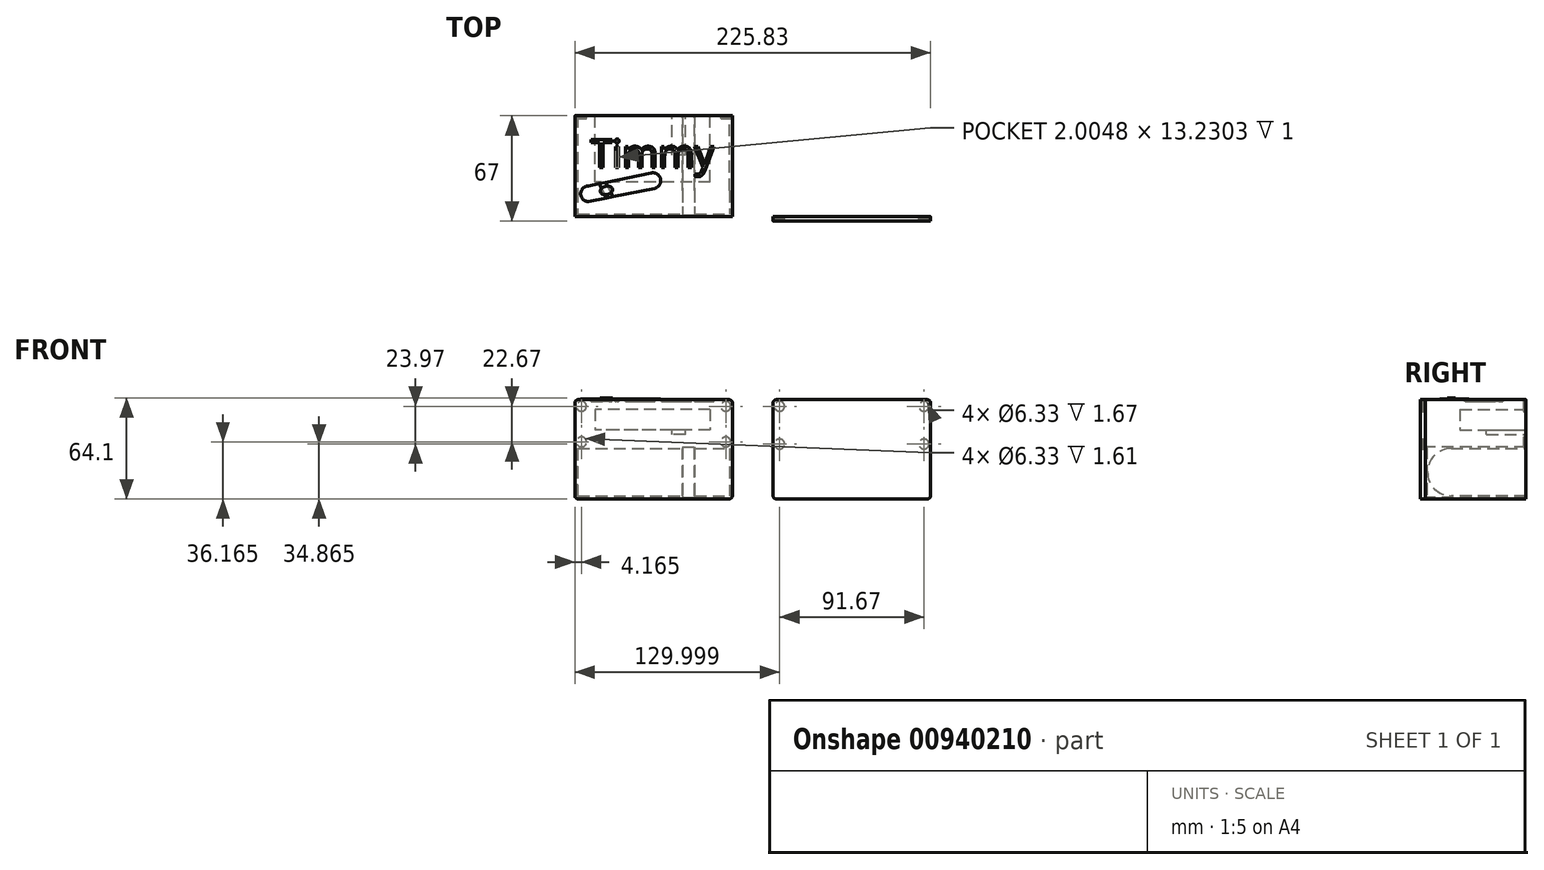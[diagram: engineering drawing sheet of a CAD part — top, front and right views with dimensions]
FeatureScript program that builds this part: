
annotation { "Feature Type Name" : "Feature", "Feature Type Description" : "" }
export const myFeature = defineFeature(function(context is Context, id is Id, definition is map)
    precondition{}
    {
        {
            var Q0;
            Q0=qCreatedBy(makeId("Top.planeOp"),FACE);
            var sketch = newSketch(context, id + "F0", { "sketchPlane" : qUnion([Q0])});
            skLineSegment(sketch, "E0.bottom", {"start": v(-100, 64) * mm, "end": v(0, 64) * mm});
            skLineSegment(sketch, "E0.top", {"start": v(-100, 0) * mm, "end": v(0, 0) * mm});
            skLineSegment(sketch, "E0.left", {"start": v(-100, 64) * mm, "end": v(-100, 0) * mm});
            skLineSegment(sketch, "E0.right", {"start": v(0, 64) * mm, "end": v(0, 0) * mm});
            skSolve(sketch);
        }
        {
            var Q0;
            Q0 = qSketchRegion(id + "F0", true);
            extrude(context, id + "F1", {"entities" : qUnion([Q0]), "depth" : 63 * mm, "offsetDistance" : 25 * mm});
        }
        {
            var Q0;
            Q0=makeQuery(id+"F1.opExtrude","SWEPT_FACE",FACE,{"disambiguationData":[OSD([sQuery(id+"F0.wireOp",EDGE,"E0.right")])]});
            var sketch = newSketch(context, id + "F2", { "sketchPlane" : qUnion([Q0])});
            skCircle(sketch, "E1", {"center": v(16.5, 17) * mm, "radius": 15 * mm});
            skCircle(sketch, "E2", {"center": v(48.5, 17) * mm, "radius": 15 * mm});
            skLineSegment(sketch, "E3", {"start": v(16.5, 32) * mm, "end": v(48.5, 32) * mm});
            skLineSegment(sketch, "E4", {"start": v(16.5, 2) * mm, "end": v(48.5, 2) * mm});
            skLineSegment(sketch, "E5", {"start": v(48.5, 32) * mm, "end": v(64, 32) * mm});
            skLineSegment(sketch, "E6", {"start": v(64, 32) * mm, "end": v(64, 2) * mm});
            skLineSegment(sketch, "E7", {"start": v(64, 2) * mm, "end": v(48.5, 2) * mm});
            skSolve(sketch);
        }
        {
            var Q0;
            Q0 = qSketchRegion(id + "F2", true);
            extrude(context, id + "F3", {"entities" : qUnion([Q0]), "operationType" : NewBodyOperationType.REMOVE, "endBound" : BoundingType.UP_TO_NEXT, "oppositeDirection" : true, "depth" : 186.6 * mm, "hasOffset" : true, "offsetDistance" : 1.75 * mm, "hasSecondDirection" : true, "secondDirectionOppositeDirection" : true, "secondDirectionDepth" : 1.75 * mm, "hasSecondDirectionOffset" : true, "secondDirectionOffsetDistance" : 2 * mm, "secondDirectionOffsetOppositeDirection" : true});
        }
        {
            var Q0;
            Q0=makeQuery(id+"F1.opExtrude","SWEPT_FACE",FACE,{"disambiguationData":[OSD([sQuery(id+"F0.wireOp",EDGE,"E0.top")])]});
            var sketch = newSketch(context, id + "F4", { "sketchPlane" : qUnion([Q0])});
            skLineSegment(sketch, "E8.bottom", {"start": v(-31.75, 33) * mm, "end": v(-23.95, 33) * mm});
            skLineSegment(sketch, "E8.top", {"start": v(-31.75, 1) * mm, "end": v(-23.95, 1) * mm});
            skLineSegment(sketch, "E8.left", {"start": v(-31.75, 33) * mm, "end": v(-31.75, 1) * mm});
            skLineSegment(sketch, "E8.right", {"start": v(-23.95, 33) * mm, "end": v(-23.95, 1) * mm});
            skLineSegment(sketch, "E9", {"start": v(0, 0) * mm, "end": v(-66.11, 0) * mm, "construction": true});
            skSolve(sketch);
        }
        {
            var Q0;
            Q0 = qSketchRegion(id + "F4", true);
            var Q1;
            Q1=makeQuery(id+"F1.opExtrude","SWEPT_FACE",FACE,{"disambiguationData":[OSD([sQuery(id+"F0.wireOp",EDGE,"E0.bottom")])]});
            var Q2;
            Q2=makeQuery(id+"F1.opExtrude","SWEPT_BODY",BODY,{"disambiguationData":[OSD([sQuery(id+"F0.wireOp",EDGE,"E0.bottom"),sQuery(id+"F0.wireOp",EDGE,"E0.top"),sQuery(id+"F0.wireOp",EDGE,"E0.left"),sQuery(id+"F0.wireOp",EDGE,"E0.right")])]});
            extrude(context, id + "F5", {"entities" : qUnion([Q0]), "operationType" : NewBodyOperationType.REMOVE, "endBound" : BoundingType.UP_TO_SURFACE, "oppositeDirection" : true, "depth" : 25 * mm, "endBoundEntityFace" : qUnion([Q1]), "endBoundEntityBody" : qUnion([Q2]), "offsetDistance" : 1 * mm, "hasSecondDirection" : true, "secondDirectionOppositeDirection" : true, "secondDirectionDepth" : 1 * mm, "hasSecondDirectionOffset" : true, "secondDirectionOffsetDistance" : 1 * mm});
        }
        {
            var Q0;
            Q0=makeQuery(id+"F1.opExtrude","SWEPT_FACE",FACE,{"disambiguationData":[OSD([sQuery(id+"F0.wireOp",EDGE,"E0.bottom")])]});
            var sketch = newSketch(context, id + "F6", { "sketchPlane" : qUnion([Q0])});
            skLineSegment(sketch, "E10.bottom", {"start": v(14.07, 56.92) * mm, "end": v(87.07, 56.92) * mm});
            skLineSegment(sketch, "E10.top", {"start": v(14.07, 43.92) * mm, "end": v(87.07, 43.92) * mm});
            skLineSegment(sketch, "E10.left", {"start": v(14.07, 56.92) * mm, "end": v(14.07, 43.92) * mm});
            skLineSegment(sketch, "E10.right", {"start": v(87.07, 56.92) * mm, "end": v(87.07, 43.92) * mm});
            skLineSegment(sketch, "E11.bottom", {"start": v(29.77, 40.92) * mm, "end": v(38.37, 40.92) * mm});
            skLineSegment(sketch, "E11.left", {"start": v(29.77, 40.92) * mm, "end": v(29.77, 43.92) * mm});
            skLineSegment(sketch, "E11.right", {"start": v(38.37, 40.92) * mm, "end": v(38.37, 43.92) * mm});
            skSolve(sketch);
        }
        {
            var Q0;
            Q0=makeQuery(id+"F6.imprint","IMPRINT",FACE,{"disambiguationData":[TD([[makeQuery(id+"F6.imprint","IMPRINT",EDGE,{"derivedFrom":sQuery(id+"F6.wireOp",EDGE,"E10.bottom")}),-1.0]])]});
            extrude(context, id + "F7", {"entities" : qUnion([Q0]), "operationType" : NewBodyOperationType.REMOVE, "oppositeDirection" : true, "depth" : 42 * mm, "offsetDistance" : 25 * mm});
        }
        {
            var Q0;
            Q0=makeQuery(id+"F6.imprint","IMPRINT",FACE,{"disambiguationData":[TD([[makeQuery(id+"F6.imprint","IMPRINT",EDGE,{"derivedFrom":sQuery(id+"F6.wireOp",EDGE,"E11.bottom")}),1.0]])]});
            extrude(context, id + "F8", {"entities" : qUnion([Q0]), "operationType" : NewBodyOperationType.REMOVE, "oppositeDirection" : true, "depth" : 25 * mm, "offsetDistance" : 25 * mm});
        }
        {
            var Q0;
            Q0=qCreatedBy(makeId("Front.planeOp"),FACE);
            var sketch = newSketch(context, id + "F9", { "sketchPlane" : qUnion([Q0])});
            skLineSegment(sketch, "E12.bottom", {"start": v(125.83, 63) * mm, "end": v(25.83, 63) * mm});
            skLineSegment(sketch, "E12.top", {"start": v(125.83, 0) * mm, "end": v(25.83, 0) * mm});
            skLineSegment(sketch, "E12.left", {"start": v(125.83, 63) * mm, "end": v(125.83, 0) * mm});
            skLineSegment(sketch, "E12.right", {"start": v(25.83, 63) * mm, "end": v(25.83, 0) * mm});
            skSolve(sketch);
        }
        {
            var Q0;
            Q0=makeQuery(id+"F9.imprint","IMPRINT",FACE,{"disambiguationData":[TD([[makeQuery(id+"F9.imprint","IMPRINT",EDGE,{"derivedFrom":sQuery(id+"F9.wireOp",EDGE,"E12.bottom")}),1.0]])]});
            extrude(context, id + "F10", {"entities" : qUnion([Q0]), "depth" : 3 * mm, "offsetDistance" : 25 * mm});
        }
        {
            var Q0;
            Q0=makeQuery(id+"F6.imprint","IMPRINT",FACE,{"disambiguationData":[TD([[makeQuery(id+"F6.imprint","IMPRINT",EDGE,{"derivedFrom":sQuery(id+"F6.wireOp",EDGE,"E10.bottom")}),1.0]])]});
            var sketch = newSketch(context, id + "F11", { "sketchPlane" : qUnion([Q0])});
            skCircle(sketch, "E13", {"center": v(95.84, 58.84) * mm, "radius": 3.17 * mm});
            skCircle(sketch, "E14", {"center": v(95.84, 36.16) * mm, "radius": 3.17 * mm});
            skCircle(sketch, "E15", {"center": v(4.16, 58.84) * mm, "radius": 3.17 * mm});
            skCircle(sketch, "E16", {"center": v(4.17, 36.16) * mm, "radius": 3.17 * mm});
            skSolve(sketch);
        }
        {
            var Q0;
            Q0 = qSketchRegion(id + "F11", true);
            extrude(context, id + "F12", {"entities" : qUnion([Q0]), "operationType" : NewBodyOperationType.REMOVE, "oppositeDirection" : true, "depth" : 1.61 * mm, "offsetDistance" : 25 * mm});
        }
        {
            var Q0;
            Q0=makeQuery(id+"F10.opExtrude","CAP_FACE",FACE,{"disambiguationData":[OSD([sQuery(id+"F9.wireOp",EDGE,"E12.bottom"),sQuery(id+"F9.wireOp",EDGE,"E12.top"),sQuery(id+"F9.wireOp",EDGE,"E12.left"),sQuery(id+"F9.wireOp",EDGE,"E12.right")])],"isStart":true});
            var sketch = newSketch(context, id + "F13", { "sketchPlane" : qUnion([Q0])});
            skCircle(sketch, "E17", {"center": v(-30, 34.87) * mm, "radius": 3.17 * mm});
            skCircle(sketch, "E18", {"center": v(-30, 58.83) * mm, "radius": 3.17 * mm});
            skCircle(sketch, "E19", {"center": v(-121.67, 58.84) * mm, "radius": 3.17 * mm});
            skCircle(sketch, "E20", {"center": v(-121.67, 34.87) * mm, "radius": 3.17 * mm});
            skSolve(sketch);
        }
        {
            var Q0;
            Q0 = qSketchRegion(id + "F13", true);
            extrude(context, id + "F14", {"entities" : qUnion([Q0]), "operationType" : NewBodyOperationType.REMOVE, "oppositeDirection" : true, "depth" : 1.67 * mm, "offsetDistance" : 25 * mm});
        }
        {
            var Q0;
            Q0=makeQuery(id+"F1.opExtrude","CAP_FACE",FACE,{"disambiguationData":[OSD([sQuery(id+"F0.wireOp",EDGE,"E0.bottom"),sQuery(id+"F0.wireOp",EDGE,"E0.top"),sQuery(id+"F0.wireOp",EDGE,"E0.left"),sQuery(id+"F0.wireOp",EDGE,"E0.right")])],"isStart":false});
            var sketch = newSketch(context, id + "F15", { "sketchPlane" : qUnion([Q0])});
            skText(sketch, "E21", { "text": "Timmy", "fontName": "OpenSans-Regular.ttf"});
            const initialGuessF15  = {"E21": [-0.09, 0.0312, 1, 0, 0.0178]};
            skSetInitialGuess(sketch, initialGuessF15);
            skSolve(sketch);
        }
        {
            var Q0;
            Q0 = qSketchRegion(id + "F15", true);
            extrude(context, id + "F16", {"entities" : qUnion([Q0]), "operationType" : NewBodyOperationType.REMOVE, "oppositeDirection" : true, "depth" : 1 * mm, "offsetDistance" : 25 * mm});
        }
        {
            var Q0;
            Q0=makeQuery(id+"F1.opExtrude","CAP_EDGE",EDGE,{"disambiguationData":[OSD([sQuery(id+"F0.wireOp",EDGE,"E0.right")])],"isStart":false});
            var Q1;
            Q1=makeQuery(id+"F1.opExtrude","CAP_EDGE",EDGE,{"disambiguationData":[OSD([sQuery(id+"F0.wireOp",EDGE,"E0.right")])],"isStart":true});
            var Q2;
            Q2=makeQuery(id+"F1.opExtrude","CAP_EDGE",EDGE,{"disambiguationData":[OSD([sQuery(id+"F0.wireOp",EDGE,"E0.left")])],"isStart":true});
            var Q3;
            Q3=makeQuery(id+"F1.opExtrude","CAP_EDGE",EDGE,{"disambiguationData":[OSD([sQuery(id+"F0.wireOp",EDGE,"E0.left")])],"isStart":false});
            var Q4;
            Q4=makeQuery(id+"F10.opExtrude","SWEPT_EDGE",EDGE,{"disambiguationData":[OSD([sQuery(id+"F9.wireOp",EDGE,"E12.bottom"),sQuery(id+"F9.wireOp",EDGE,"E12.left")])]});
            var Q5;
            Q5=makeQuery(id+"F10.opExtrude","SWEPT_EDGE",EDGE,{"disambiguationData":[OSD([sQuery(id+"F9.wireOp",EDGE,"E12.top"),sQuery(id+"F9.wireOp",EDGE,"E12.left")])]});
            var Q6;
            Q6=makeQuery(id+"F10.opExtrude","SWEPT_EDGE",EDGE,{"disambiguationData":[OSD([sQuery(id+"F9.wireOp",EDGE,"E12.top"),sQuery(id+"F9.wireOp",EDGE,"E12.right")])]});
            var Q7;
            Q7=makeQuery(id+"F10.opExtrude","SWEPT_EDGE",EDGE,{"disambiguationData":[OSD([sQuery(id+"F9.wireOp",EDGE,"E12.bottom"),sQuery(id+"F9.wireOp",EDGE,"E12.right")])]});
            fillet(context, id + "F17", {"entities" : qUnion([Q0, Q1, Q2, Q3, Q4, Q5, Q6, Q7]), "radius" : 2 * mm, "tangentPropagation" : true, "allowEdgeOverflow" : false});
        }
        {
            var Q0;
            Q0=makeQuery(id+"F1.opExtrude","CAP_FACE",FACE,{"disambiguationData":[OSD([sQuery(id+"F0.wireOp",EDGE,"E0.bottom"),sQuery(id+"F0.wireOp",EDGE,"E0.top"),sQuery(id+"F0.wireOp",EDGE,"E0.left"),sQuery(id+"F0.wireOp",EDGE,"E0.right")])],"isStart":false});
            var sketch = newSketch(context, id + "F18", { "sketchPlane" : qUnion([Q0])});
            skCircle(sketch, "E22", {"center": v(-91.34, 14.47) * mm, "radius": 5 * mm});
            skCircle(sketch, "E23", {"center": v(-50.5, 22.82) * mm, "radius": 5 * mm});
            skLineSegment(sketch, "E24", {"start": v(-91.34, 19.47) * mm, "end": v(-51.52, 27.71) * mm});
            skLineSegment(sketch, "E25", {"start": v(-91.34, 9.47) * mm, "end": v(-49.51, 17.91) * mm});
            skEllipse(sketch, "E26", {"center": v(-80.06, 16.62) * mm, "majorRadius": 2.5 * mm, "minorRadius": 2 * mm, "majorAxis": v(0.48, -0.88)});
            skLineSegment(sketch, "E27", {"start": v(-79.8, 11.8) * mm, "end": v(-84.53, 20.88) * mm});
            skLineSegment(sketch, "E28", {"start": v(-80.46, 21.72) * mm, "end": v(-75.72, 12.62) * mm});
            skSolve(sketch);
        }
        {
            var Q0;
            {var subQ0=sQuery(id+"F18.wireOp",EDGE,"E25");var subQ1=sQuery(id+"F18.wireOp",EDGE,"E22");var subQ2=makeQuery(id+"F18.imprint","INTERSECT",VERTEX,{"disambiguationData":[OD(0.0)],"derivedFrom":[subQ1,subQ0]});Q0=makeQuery(id+"F18.imprint","IMPRINT",FACE,{"disambiguationData":[TD([[makeQuery(id+"F18.imprint","IMPRINT",EDGE,{"disambiguationData":[TD([[subQ2,-1.0]])],"derivedFrom":subQ1}),1.0]])]});}
            var Q1;
            {var subQ0=sQuery(id+"F18.wireOp",EDGE,"E23");var subQ1=makeQuery(id+"F18.imprint","INTERSECT",VERTEX,{"derivedFrom":[subQ0,sQuery(id+"F18.wireOp",EDGE,"E24")]});Q1=makeQuery(id+"F18.imprint","IMPRINT",FACE,{"disambiguationData":[TD([[makeQuery(id+"F18.imprint","IMPRINT",EDGE,{"disambiguationData":[TD([[subQ1,-1.0]])],"derivedFrom":subQ0}),1.0]])]});}
            var Q2;
            {var subQ0=sQuery(id+"F18.wireOp",EDGE,"E22");var subQ1=makeQuery(id+"F18.imprint","INTERSECT",VERTEX,{"derivedFrom":[subQ0,sQuery(id+"F18.wireOp",EDGE,"E24")]});Q2=makeQuery(id+"F18.imprint","IMPRINT",FACE,{"disambiguationData":[TD([[makeQuery(id+"F18.imprint","IMPRINT",EDGE,{"disambiguationData":[TD([[subQ1,-1.0]])],"derivedFrom":subQ0}),1.0]])]});}
            var Q3;
            {var subQ4=sQuery(id+"F18.wireOp",EDGE,"E22");var subQ6=sQuery(id+"F18.wireOp",EDGE,"E24");var subQ7=makeQuery(id+"F18.imprint","INTERSECT",VERTEX,{"derivedFrom":[subQ4,subQ6]});Q3=makeQuery(id+"F18.imprint","IMPRINT",FACE,{"disambiguationData":[TD([[makeQuery(id+"F18.imprint","IMPRINT",EDGE,{"disambiguationData":[TD([[subQ7,1.0]])],"derivedFrom":subQ4}),-1.0]])]});}
            var Q4;
            {var subQ1=sQuery(id+"F18.wireOp",EDGE,"E24");var subQ5=sQuery(id+"F18.wireOp",EDGE,"E23");var subQ8=makeQuery(id+"F18.imprint","INTERSECT",VERTEX,{"derivedFrom":[subQ5,subQ1]});Q4=makeQuery(id+"F18.imprint","IMPRINT",FACE,{"disambiguationData":[TD([[makeQuery(id+"F18.imprint","IMPRINT",EDGE,{"disambiguationData":[TD([[subQ8,-1.0]])],"derivedFrom":subQ5}),-1.0]])]});}
            extrude(context, id + "F19", {"entities" : qUnion([Q0, Q1, Q2, Q3, Q4]), "operationType" : NewBodyOperationType.ADD, "depth" : .5 * mm, "offsetDistance" : 25 * mm});
        }
        {
            var Q0;
            {var subQ0=sQuery(id+"F18.wireOp",EDGE,"E27");var subQ1=sQuery(id+"F18.wireOp",EDGE,"E24");var subQ2=makeQuery(id+"F18.imprint","INTERSECT",VERTEX,{"derivedFrom":[subQ1,subQ0]});Q0=makeQuery(id+"F18.imprint","IMPRINT",FACE,{"disambiguationData":[TD([[makeQuery(id+"F18.imprint","IMPRINT",EDGE,{"disambiguationData":[TD([[subQ2,-1.0]])],"derivedFrom":subQ1}),-1.0]])]});}
            var Q1;
            {var subQ0=sQuery(id+"F18.wireOp",EDGE,"E27");var subQ1=sQuery(id+"F18.wireOp",EDGE,"E25");var subQ2=makeQuery(id+"F18.imprint","INTERSECT",VERTEX,{"derivedFrom":[subQ1,subQ0]});Q1=makeQuery(id+"F18.imprint","IMPRINT",FACE,{"disambiguationData":[TD([[makeQuery(id+"F18.imprint","IMPRINT",EDGE,{"disambiguationData":[TD([[subQ2,-1.0]])],"derivedFrom":subQ1}),1.0]])]});}
            var Q2;
            {var subQ0=sQuery(id+"F18.wireOp",EDGE,"E26");var subQ1=makeQuery(id+"F18.imprint","INTERSECT",VERTEX,{"derivedFrom":[subQ0,sQuery(id+"F18.wireOp",EDGE,"E27")]});Q2=makeQuery(id+"F18.imprint","IMPRINT",FACE,{"disambiguationData":[TD([[makeQuery(id+"F18.imprint","IMPRINT",EDGE,{"disambiguationData":[TD([[subQ1,1.0]])],"derivedFrom":subQ0}),1.0]])]});}
            extrude(context, id + "F20", {"entities" : qUnion([Q0, Q1, Q2]), "operationType" : NewBodyOperationType.ADD, "depth" : .6 * mm, "offsetDistance" : 25 * mm});
        }
        {
            var Q0;
            Q0=makeQuery(id+"F20.opExtrude","CAP_FACE",FACE,{"disambiguationData":[OSD([sQuery(id+"F18.wireOp",EDGE,"E24"),sQuery(id+"F18.wireOp",EDGE,"E25"),sQuery(id+"F18.wireOp",EDGE,"E27"),sQuery(id+"F18.wireOp",EDGE,"E28")])],"isStart":false});
            var sketch = newSketch(context, id + "F21", { "sketchPlane" : qUnion([Q0])});
            skEllipse(sketch, "E29", {"center": v(-80.1, 16.63) * mm, "majorRadius": 3.98 * mm, "minorRadius": 2.61 * mm, "majorAxis": v(0.98, 0.2)});
            skSolve(sketch);
        }
        {
            var Q0;
            Q0 = qSketchRegion(id + "F21", true);
            extrude(context, id + "F22", {"entities" : qUnion([Q0]), "operationType" : NewBodyOperationType.ADD, "depth" : .5 * mm, "offsetDistance" : 25 * mm});
        }
    });
